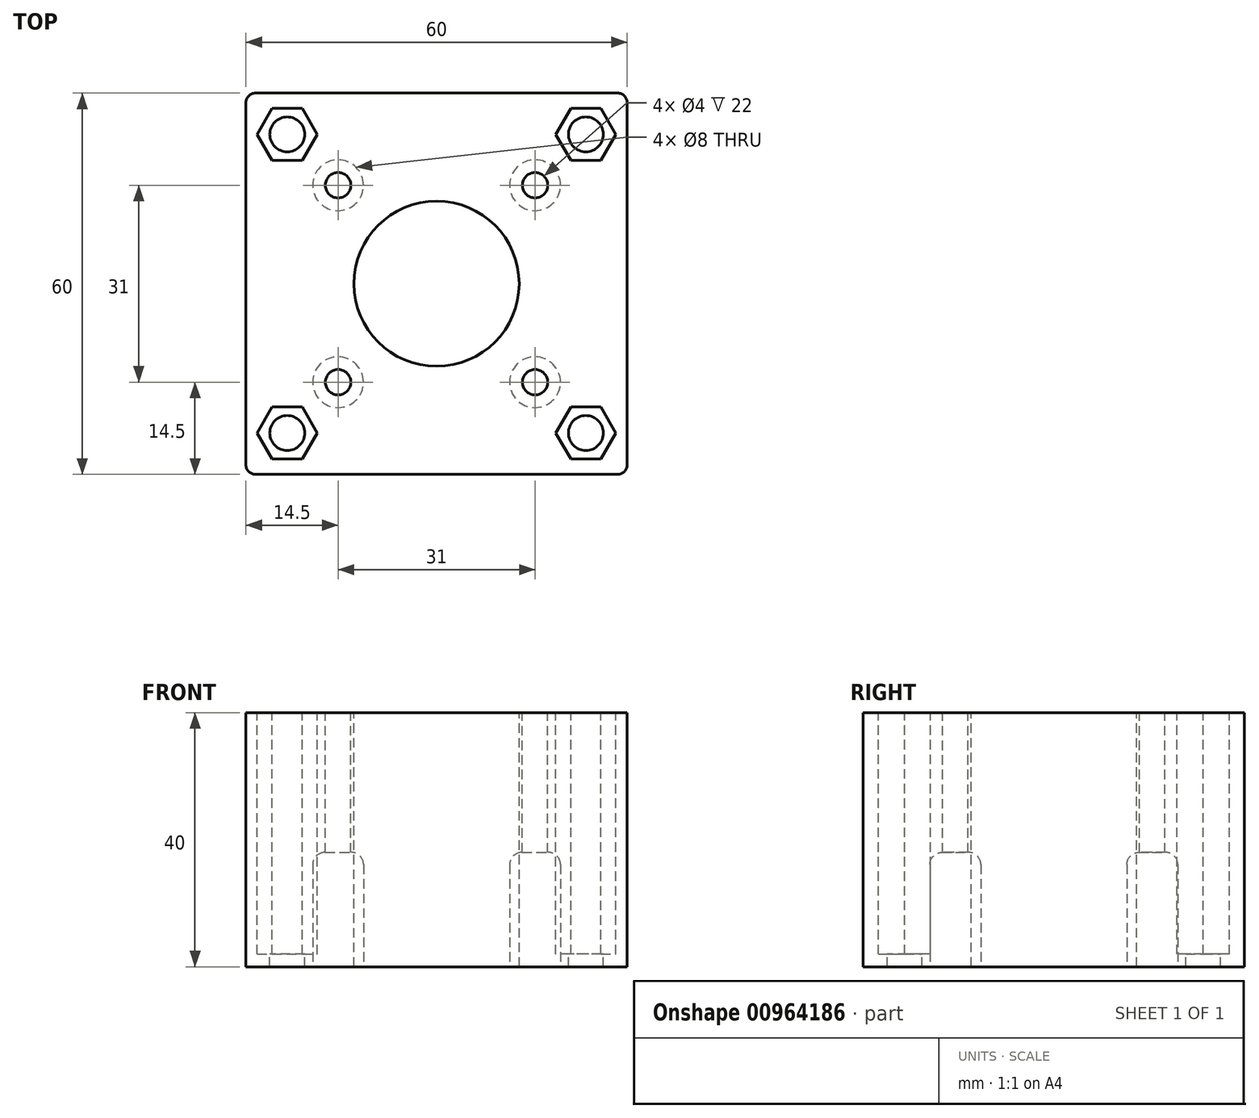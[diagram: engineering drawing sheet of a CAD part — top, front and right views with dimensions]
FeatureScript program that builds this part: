
annotation { "Feature Type Name" : "Feature", "Feature Type Description" : "" }
export const myFeature = defineFeature(function(context is Context, id is Id, definition is map)
    precondition{}
    {
        {
            var Q0;
            Q0=qCreatedBy(makeId("Top.planeOp"),FACE);
            var sketch = newSketch(context, id + "F0", { "sketchPlane" : qUnion([Q0])});
            skLineSegment(sketch, "E0.bottom", {"start": v(-30, 30) * mm, "end": v(30, 30) * mm});
            skLineSegment(sketch, "E0.top", {"start": v(-30, -30) * mm, "end": v(30, -30) * mm});
            skLineSegment(sketch, "E0.left", {"start": v(-30, 30) * mm, "end": v(-30, -30) * mm});
            skLineSegment(sketch, "E0.right", {"start": v(30, 30) * mm, "end": v(30, -30) * mm});
            skSolve(sketch);
        }
        {
            var Q0;
            Q0 = qSketchRegion(id + "F0", true);
            extrude(context, id + "F1", {"entities" : qUnion([Q0]), "depth" : 40 * mm, "offsetDistance" : 25 * mm});
        }
        {
            var Q0;
            Q0=makeQuery(id+"F1.opExtrude","CAP_FACE",FACE,{"disambiguationData":[OSD([sQuery(id+"F0.wireOp",EDGE,"E0.bottom"),sQuery(id+"F0.wireOp",EDGE,"E0.top"),sQuery(id+"F0.wireOp",EDGE,"E0.left"),sQuery(id+"F0.wireOp",EDGE,"E0.right")])],"isStart":false});
            var sketch = newSketch(context, id + "F2", { "sketchPlane" : qUnion([Q0])});
            skCircle(sketch, "E1", {"center": v(-23.5, 23.5) * mm, "radius": 2.75 * mm});
            skCircle(sketch, "E2.MirrorC", {"center": v(23.5, 23.5) * mm, "radius": 2.75 * mm});
            skCircle(sketch, "E3.MirrorC", {"center": v(23.5, -23.5) * mm, "radius": 2.75 * mm});
            skCircle(sketch, "E4.MirrorC", {"center": v(-23.5, -23.5) * mm, "radius": 2.75 * mm});
            skSolve(sketch);
        }
        {
            var Q0;
            Q0 = qSketchRegion(id + "F2", true);
            extrude(context, id + "F3", {"entities" : qUnion([Q0]), "operationType" : NewBodyOperationType.REMOVE, "endBound" : BoundingType.UP_TO_NEXT, "oppositeDirection" : true, "depth" : 25 * mm, "offsetDistance" : 25 * mm});
        }
        {
            var Q0;
            Q0=makeQuery(id+"F1.opExtrude","CAP_FACE",FACE,{"disambiguationData":[OSD([sQuery(id+"F0.wireOp",EDGE,"E0.bottom"),sQuery(id+"F0.wireOp",EDGE,"E0.top"),sQuery(id+"F0.wireOp",EDGE,"E0.left"),sQuery(id+"F0.wireOp",EDGE,"E0.right")])],"isStart":false});
            var sketch = newSketch(context, id + "F4", { "sketchPlane" : qUnion([Q0])});
            skCircle(sketch, "E5", {"center": v(-15.5, 15.5) * mm, "radius": 2 * mm});
            skCircle(sketch, "E6.MirrorC", {"center": v(15.5, 15.5) * mm, "radius": 2 * mm});
            skCircle(sketch, "E7.MirrorC", {"center": v(15.5, -15.5) * mm, "radius": 2 * mm});
            skCircle(sketch, "E8.MirrorC", {"center": v(-15.5, -15.5) * mm, "radius": 2 * mm});
            skSolve(sketch);
        }
        {
            var Q0;
            Q0 = qSketchRegion(id + "F4", true);
            extrude(context, id + "F5", {"entities" : qUnion([Q0]), "operationType" : NewBodyOperationType.REMOVE, "endBound" : BoundingType.UP_TO_NEXT, "oppositeDirection" : true, "depth" : 25 * mm, "offsetDistance" : 25 * mm});
        }
        {
            var Q0;
            Q0=makeQuery(id+"F1.opExtrude","CAP_FACE",FACE,{"disambiguationData":[OSD([sQuery(id+"F0.wireOp",EDGE,"E0.bottom"),sQuery(id+"F0.wireOp",EDGE,"E0.top"),sQuery(id+"F0.wireOp",EDGE,"E0.left"),sQuery(id+"F0.wireOp",EDGE,"E0.right")])],"isStart":false});
            var sketch = newSketch(context, id + "F6", { "sketchPlane" : qUnion([Q0])});
            skCircle(sketch, "E9", {"center": v(0, 0) * mm, "radius": 13 * mm});
            skSolve(sketch);
        }
        {
            var Q0;
            Q0 = qSketchRegion(id + "F6", true);
            extrude(context, id + "F7", {"entities" : qUnion([Q0]), "operationType" : NewBodyOperationType.REMOVE, "endBound" : BoundingType.UP_TO_NEXT, "oppositeDirection" : true, "depth" : 25 * mm, "offsetDistance" : 25 * mm});
        }
        {
            var Q0;
            Q0=makeQuery(id+"F1.opExtrude","SWEPT_EDGE",EDGE,{"disambiguationData":[OSD([sQuery(id+"F0.wireOp",EDGE,"E0.top"),sQuery(id+"F0.wireOp",EDGE,"E0.right")])]});
            var Q1;
            Q1=makeQuery(id+"F1.opExtrude","SWEPT_EDGE",EDGE,{"disambiguationData":[OSD([sQuery(id+"F0.wireOp",EDGE,"E0.top"),sQuery(id+"F0.wireOp",EDGE,"E0.left")])]});
            var Q2;
            Q2=makeQuery(id+"F1.opExtrude","SWEPT_EDGE",EDGE,{"disambiguationData":[OSD([sQuery(id+"F0.wireOp",EDGE,"E0.bottom"),sQuery(id+"F0.wireOp",EDGE,"E0.left")])]});
            var Q3;
            Q3=makeQuery(id+"F1.opExtrude","SWEPT_EDGE",EDGE,{"disambiguationData":[OSD([sQuery(id+"F0.wireOp",EDGE,"E0.bottom"),sQuery(id+"F0.wireOp",EDGE,"E0.right")])]});
            fillet(context, id + "F8", {"entities" : qUnion([Q0, Q1, Q2, Q3]), "radius" : 1.5 * mm, "tangentPropagation" : true, "allowEdgeOverflow" : false});
        }
        {
            var Q0;
            Q0=makeQuery(id+"F1.opExtrude","CAP_FACE",FACE,{"disambiguationData":[OSD([sQuery(id+"F0.wireOp",EDGE,"E0.bottom"),sQuery(id+"F0.wireOp",EDGE,"E0.top"),sQuery(id+"F0.wireOp",EDGE,"E0.left"),sQuery(id+"F0.wireOp",EDGE,"E0.right")])],"isStart":false});
            var sketch = newSketch(context, id + "F9", { "sketchPlane" : qUnion([Q0])});
            skCircle(sketch, "E10.0", {"center": v(23.5, 23.5) * mm, "radius": 2.75 * mm});
            skCircle(sketch, "E11.cCircle", {"center": v(23.5, 23.5) * mm, "radius": 4.1 * mm, "construction": true});
            skLineSegment(sketch, "E11.0", {"start": v(25.87, 19.4) * mm, "end": v(21.13, 19.4) * mm});
            skLineSegment(sketch, "E11.1", {"start": v(21.13, 19.4) * mm, "end": v(18.77, 23.5) * mm});
            skLineSegment(sketch, "E11.2", {"start": v(18.77, 23.5) * mm, "end": v(21.13, 27.6) * mm});
            skLineSegment(sketch, "E11.3", {"start": v(21.13, 27.6) * mm, "end": v(25.87, 27.6) * mm});
            skLineSegment(sketch, "E11.4", {"start": v(25.87, 27.6) * mm, "end": v(28.23, 23.5) * mm});
            skLineSegment(sketch, "E11.5", {"start": v(28.23, 23.5) * mm, "end": v(25.87, 19.4) * mm});
            skPoint(sketch, "E11.0.midPoint", {"position": v(23.5, 19.4) * mm});
            skLineSegment(sketch, "E12.MirrorCS", {"start": v(-21.13, 19.4) * mm, "end": v(-18.77, 23.5) * mm});
            skLineSegment(sketch, "E13.MirrorCS", {"start": v(-18.77, 23.5) * mm, "end": v(-21.13, 27.6) * mm});
            skLineSegment(sketch, "E14.MirrorCS", {"start": v(-25.87, 19.4) * mm, "end": v(-21.13, 19.4) * mm});
            skLineSegment(sketch, "E15.MirrorCS", {"start": v(-28.23, 23.5) * mm, "end": v(-25.87, 19.4) * mm});
            skLineSegment(sketch, "E16.MirrorCS", {"start": v(-21.13, 27.6) * mm, "end": v(-25.87, 27.6) * mm});
            skLineSegment(sketch, "E17.MirrorCS", {"start": v(-25.87, 27.6) * mm, "end": v(-28.23, 23.5) * mm});
            skPoint(sketch, "E18.MirrorP", {"position": v(-23.5, 19.4) * mm});
            skLineSegment(sketch, "E19.MirrorCS", {"start": v(21.13, -19.4) * mm, "end": v(18.77, -23.5) * mm});
            skLineSegment(sketch, "E20.MirrorCS", {"start": v(25.87, -19.4) * mm, "end": v(21.13, -19.4) * mm});
            skLineSegment(sketch, "E21.MirrorCS", {"start": v(18.77, -23.5) * mm, "end": v(21.13, -27.6) * mm});
            skLineSegment(sketch, "E22.MirrorCS", {"start": v(28.23, -23.5) * mm, "end": v(25.87, -19.4) * mm});
            skLineSegment(sketch, "E23.MirrorCS", {"start": v(25.87, -27.6) * mm, "end": v(28.23, -23.5) * mm});
            skPoint(sketch, "E24.MirrorP", {"position": v(23.5, -19.4) * mm});
            skLineSegment(sketch, "E25.MirrorCS", {"start": v(21.13, -27.6) * mm, "end": v(25.87, -27.6) * mm});
            skLineSegment(sketch, "E26.MirrorCS", {"start": v(-25.87, -19.4) * mm, "end": v(-21.13, -19.4) * mm});
            skPoint(sketch, "E27.MirrorP", {"position": v(-23.5, -19.4) * mm});
            skLineSegment(sketch, "E28.MirrorCS", {"start": v(-18.77, -23.5) * mm, "end": v(-21.13, -27.6) * mm});
            skLineSegment(sketch, "E29.MirrorCS", {"start": v(-21.13, -19.4) * mm, "end": v(-18.77, -23.5) * mm});
            skLineSegment(sketch, "E30.MirrorCS", {"start": v(-28.23, -23.5) * mm, "end": v(-25.87, -19.4) * mm});
            skLineSegment(sketch, "E31.MirrorCS", {"start": v(-25.87, -27.6) * mm, "end": v(-28.23, -23.5) * mm});
            skLineSegment(sketch, "E32.MirrorCS", {"start": v(-21.13, -27.6) * mm, "end": v(-25.87, -27.6) * mm});
            skSolve(sketch);
        }
        {
            var Q0;
            Q0 = qSketchRegion(id + "F9", true);
            extrude(context, id + "F10", {"entities" : qUnion([Q0]), "operationType" : NewBodyOperationType.REMOVE, "oppositeDirection" : true, "depth" : 38 * mm, "offsetDistance" : 25 * mm});
        }
        {
            var Q0;
            Q0=makeQuery(id+"F1.opExtrude","CAP_FACE",FACE,{"disambiguationData":[OSD([sQuery(id+"F0.wireOp",EDGE,"E0.bottom"),sQuery(id+"F0.wireOp",EDGE,"E0.top"),sQuery(id+"F0.wireOp",EDGE,"E0.left"),sQuery(id+"F0.wireOp",EDGE,"E0.right")])],"isStart":true});
            var sketch = newSketch(context, id + "F11", { "sketchPlane" : qUnion([Q0])});
            skCircle(sketch, "E33.0", {"center": v(15.5, 15.5) * mm, "radius": 2 * mm});
            skCircle(sketch, "E34", {"center": v(15.5, 15.5) * mm, "radius": 4 * mm});
            skCircle(sketch, "E35.MirrorC", {"center": v(-15.5, 15.5) * mm, "radius": 4 * mm});
            skCircle(sketch, "E36.MirrorC", {"center": v(-15.5, -15.5) * mm, "radius": 4 * mm});
            skCircle(sketch, "E37.MirrorC", {"center": v(15.5, -15.5) * mm, "radius": 4 * mm});
            skSolve(sketch);
        }
        {
            var Q0;
            Q0 = qSketchRegion(id + "F11", true);
            extrude(context, id + "F12", {"entities" : qUnion([Q0]), "operationType" : NewBodyOperationType.REMOVE, "oppositeDirection" : true, "depth" : 18 * mm, "offsetDistance" : 25 * mm});
        }
        {
            var Q0;
            Q0=makeQuery(id+"F12.boolean.opBoolean","COPY",EDGE,{"derivedFrom":makeQuery(id+"F12.opExtrude","CAP_EDGE",EDGE,{"disambiguationData":[OSD([sQuery(id+"F11.wireOp",EDGE,"E37.MirrorC")])],"isStart":false})});
            var Q1;
            Q1=makeQuery(id+"F12.boolean.opBoolean","COPY",EDGE,{"derivedFrom":makeQuery(id+"F12.opExtrude","CAP_EDGE",EDGE,{"disambiguationData":[OSD([sQuery(id+"F11.wireOp",EDGE,"E36.MirrorC")])],"isStart":false})});
            var Q2;
            Q2=makeQuery(id+"F12.boolean.opBoolean","COPY",EDGE,{"derivedFrom":makeQuery(id+"F12.opExtrude","CAP_EDGE",EDGE,{"disambiguationData":[OSD([sQuery(id+"F11.wireOp",EDGE,"E34")])],"isStart":false})});
            var Q3;
            Q3=makeQuery(id+"F12.boolean.opBoolean","COPY",EDGE,{"derivedFrom":makeQuery(id+"F12.opExtrude","CAP_EDGE",EDGE,{"disambiguationData":[OSD([sQuery(id+"F11.wireOp",EDGE,"E35.MirrorC")])],"isStart":false})});
            fillet(context, id + "F13", {"entities" : qUnion([Q0, Q1, Q2, Q3]), "radius" : 1.9 * mm, "tangentPropagation" : true, "allowEdgeOverflow" : false});
        }
    });
